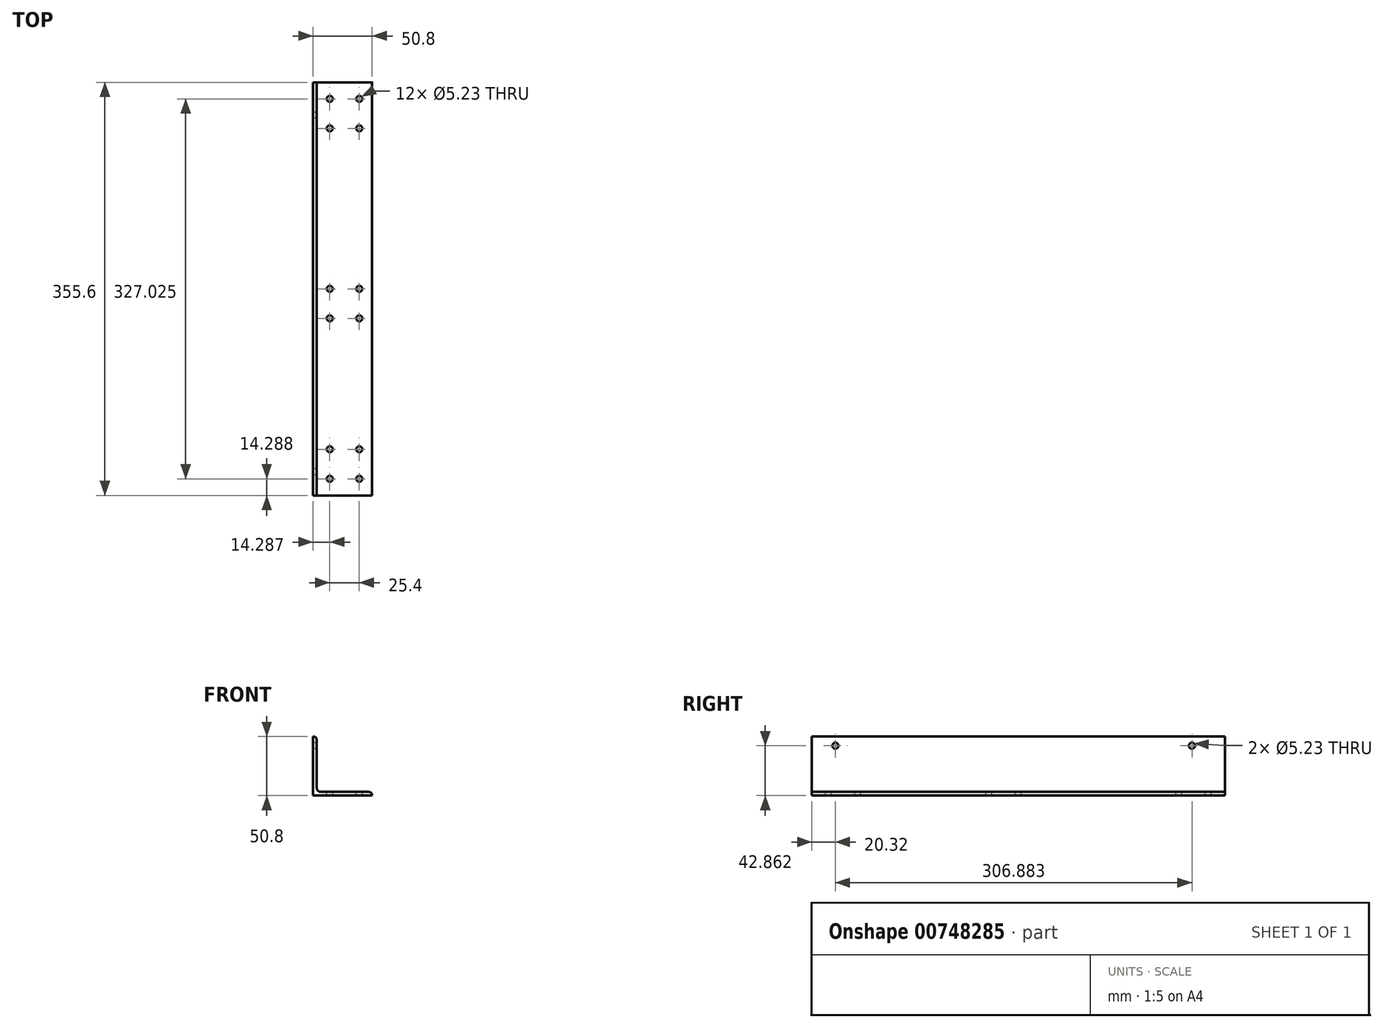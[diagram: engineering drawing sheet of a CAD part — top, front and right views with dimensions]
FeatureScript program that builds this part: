
annotation { "Feature Type Name" : "Feature", "Feature Type Description" : "" }
export const myFeature = defineFeature(function(context is Context, id is Id, definition is map)
    precondition{}
    {
        {
            var Q0;
            Q0=qCreatedBy(makeId("Front.planeOp"),FACE);
            var sketch = newSketch(context, id + "F0", { "sketchPlane" : qUnion([Q0])});
            skLineSegment(sketch, "E0", {"start": v(0, 0) * mm, "end": v(-50.8, 0) * mm});
            skLineSegment(sketch, "E1", {"start": v(-50.8, 0) * mm, "end": v(-50.8, 50.8) * mm});
            skLineSegment(sketch, "E2", {"start": v(-50.8, 50.8) * mm, "end": v(-50.8, 50.8) * mm});
            skLineSegment(sketch, "E3", {"start": v(-47.63, 47.63) * mm, "end": v(-47.63, 6.35) * mm});
            skLineSegment(sketch, "E4", {"start": v(-44.45, 3.18) * mm, "end": v(-3.18, 3.18) * mm});
            skLineSegment(sketch, "E5", {"start": v(0, 0) * mm, "end": v(0, 0) * mm});
            skPoint(sketch, "E6.visualSharp", {"position": v(-47.63, 3.18) * mm});
            skArc(sketch, "E6.filletArc", {"start": v(-47.63, 6.35) * mm, "mid": v(-46.7, 4.1) * mm, "end": v(-44.45, 3.18) * mm});
            skPoint(sketch, "E7.visualSharp", {"position": v(-47.63, 50.8) * mm});
            skArc(sketch, "E7.filletArc", {"start": v(-47.63, 47.63) * mm, "mid": v(-48.55, 49.87) * mm, "end": v(-50.8, 50.8) * mm});
            skPoint(sketch, "E8.visualSharp", {"position": v(0, 3.18) * mm});
            skArc(sketch, "E8.filletArc", {"start": v(0, 0) * mm, "mid": v(-0.93, 2.25) * mm, "end": v(-3.18, 3.18) * mm});
            skSolve(sketch);
        }
        {
            var Q0;
            Q0=qSketchRegion(id+"F0",true);
            extrude(context, id + "F1", {"entities" : qUnion([Q0]), "depth" : 355.6 * mm, "offsetDistance" : 25.4 * mm});
        }
        {
            var Q0;
            Q0=makeQuery(id+"F1.opExtrude","SWEPT_FACE",FACE,{"disambiguationData":[OSD([sQuery(id+"F0.wireOp",EDGE,"E4")])]});
            var sketch = newSketch(context, id + "F2", { "sketchPlane" : qUnion([Q0])});
            skLineSegment(sketch, "E9", {"start": v(-23.81, -355.6) * mm, "end": v(-23.81, 0) * mm, "construction": true});
            skLineSegment(sketch, "E10", {"start": v(-3.18, -341.31) * mm, "end": v(-44.45, -341.31) * mm, "construction": true});
            skCircle(sketch, "E11", {"center": v(-36.51, -341.31) * mm, "radius": 2.62 * mm});
            skLineSegment(sketch, "E12", {"start": v(-44.45, -14.29) * mm, "end": v(-3.18, -14.29) * mm, "construction": true});
            skCircle(sketch, "E13", {"center": v(-36.51, -14.29) * mm, "radius": 2.62 * mm});
            skLineSegment(sketch, "E14", {"start": v(-3.18, -177.8) * mm, "end": v(-44.45, -177.8) * mm, "construction": true});
            skLineSegment(sketch, "E15.0", {"start": v(-3.17, -98.43) * mm, "end": v(-19.05, -98.43) * mm, "construction": true});
            skCircle(sketch, "E16", {"center": v(-36.51, -177.8) * mm, "radius": 2.62 * mm});
            skLineSegment(sketch, "E17", {"start": v(-36.51, -355.6) * mm, "end": v(-36.51, 0) * mm, "construction": true});
            skLineSegment(sketch, "E18", {"start": v(-11.11, -355.6) * mm, "end": v(-11.11, 0) * mm, "construction": true});
            skCircle(sketch, "E19", {"center": v(-11.11, -14.29) * mm, "radius": 2.62 * mm});
            skLineSegment(sketch, "E20", {"start": v(-44.45, -203.2) * mm, "end": v(-3.18, -203.2) * mm, "construction": true});
            skCircle(sketch, "E21", {"center": v(-36.51, -203.2) * mm, "radius": 2.62 * mm});
            skCircle(sketch, "E22", {"center": v(-11.11, -203.2) * mm, "radius": 2.62 * mm});
            skCircle(sketch, "E23", {"center": v(-11.11, -177.8) * mm, "radius": 2.62 * mm});
            skCircle(sketch, "E24", {"center": v(-11.11, -341.31) * mm, "radius": 2.62 * mm});
            skLineSegment(sketch, "E25", {"start": v(-3.18, -315.91) * mm, "end": v(-44.45, -315.91) * mm, "construction": true});
            skCircle(sketch, "E26", {"center": v(-11.11, -315.91) * mm, "radius": 2.62 * mm});
            skCircle(sketch, "E27", {"center": v(-36.51, -315.91) * mm, "radius": 2.62 * mm});
            skLineSegment(sketch, "E28", {"start": v(-3.18, -39.69) * mm, "end": v(-44.45, -39.69) * mm, "construction": true});
            skCircle(sketch, "E29", {"center": v(-11.11, -39.69) * mm, "radius": 2.62 * mm});
            skCircle(sketch, "E30", {"center": v(-36.51, -39.69) * mm, "radius": 2.62 * mm});
            skSolve(sketch);
        }
        {
            var Q0;
            Q0=qSketchRegion(id+"F2",true);
            extrude(context, id + "F3", {"entities" : qUnion([Q0]), "operationType" : NewBodyOperationType.REMOVE, "endBound" : BoundingType.THROUGH_ALL, "oppositeDirection" : true, "depth" : 25.4 * mm, "offsetDistance" : 25.4 * mm});
        }
        {
            var Q0;
            Q0=makeQuery(id+"F1.opExtrude","SWEPT_FACE",FACE,{"disambiguationData":[OSD([sQuery(id+"F0.wireOp",EDGE,"E1")])]});
            var sketch = newSketch(context, id + "F4", { "sketchPlane" : qUnion([Q0])});
            skLineSegment(sketch, "E31", {"start": v(0, 42.86) * mm, "end": v(355.6, 42.86) * mm, "construction": true});
            skCircle(sketch, "E32", {"center": v(28.4, 42.86) * mm, "radius": 2.62 * mm});
            skCircle(sketch, "E33", {"center": v(335.28, 42.86) * mm, "radius": 2.62 * mm});
            skSolve(sketch);
        }
        {
            var Q0;
            Q0 = qSketchRegion(id + "F4", true);
            extrude(context, id + "F5", {"entities" : qUnion([Q0]), "operationType" : NewBodyOperationType.REMOVE, "endBound" : BoundingType.THROUGH_ALL, "oppositeDirection" : true, "depth" : 25.4 * mm, "offsetDistance" : 25.4 * mm});
        }
    });
